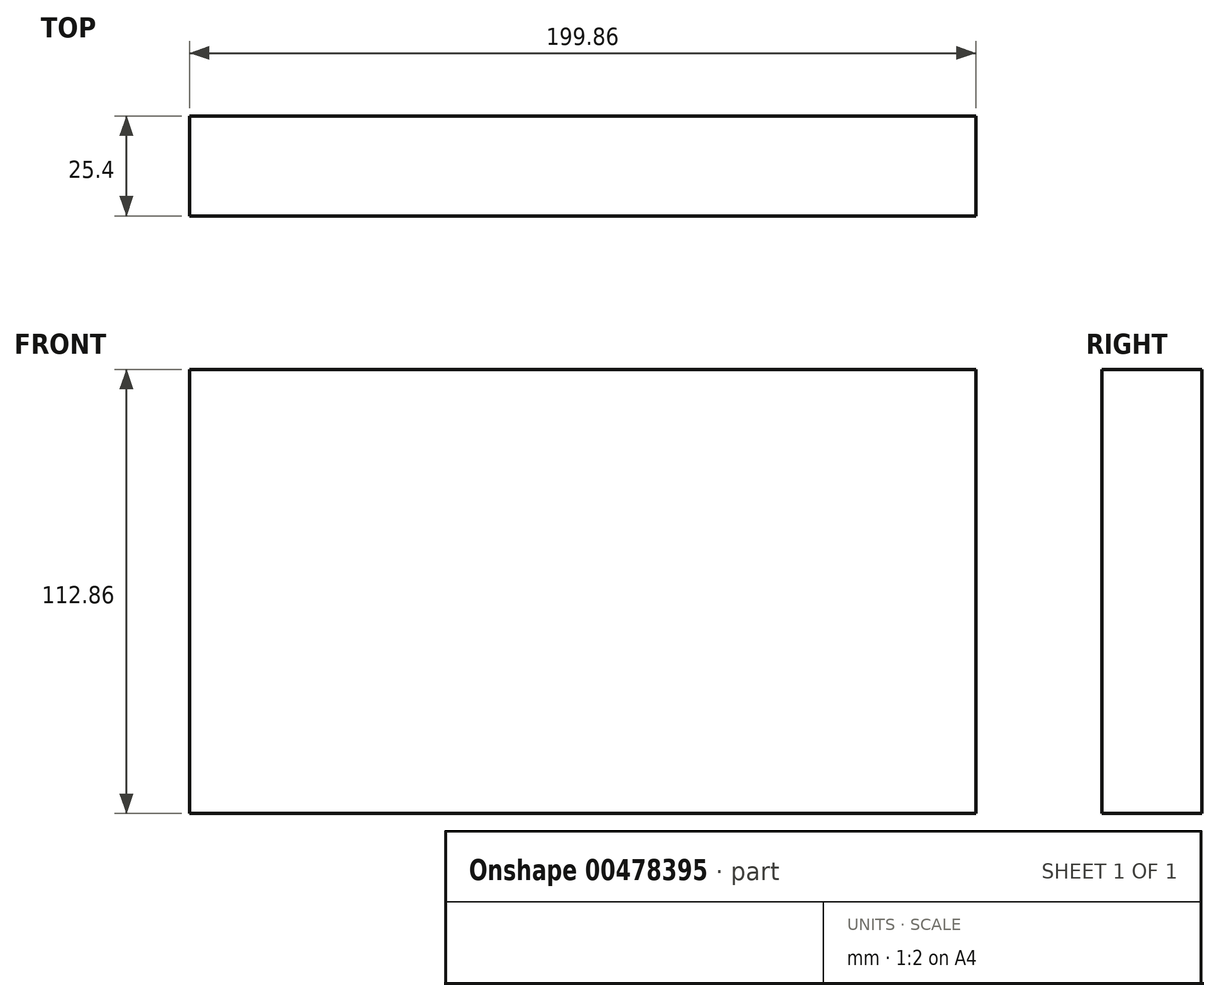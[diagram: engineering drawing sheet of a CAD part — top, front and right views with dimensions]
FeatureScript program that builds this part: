
annotation { "Feature Type Name" : "Feature", "Feature Type Description" : "" }
export const myFeature = defineFeature(function(context is Context, id is Id, definition is map)
    precondition{}
    {
        {
            var Q0;
            Q0=qCreatedBy(makeId("Front.planeOp"),FACE);
            var sketch = newSketch(context, id + "F0", { "sketchPlane" : qUnion([Q0])});
            skLineSegment(sketch, "E0.bottom", {"start": v(-97.72, 53.52) * mm, "end": v(102.14, 53.52) * mm});
            skLineSegment(sketch, "E0.top", {"start": v(-97.72, -59.34) * mm, "end": v(102.14, -59.34) * mm});
            skLineSegment(sketch, "E0.left", {"start": v(-97.72, 53.52) * mm, "end": v(-97.72, -59.34) * mm});
            skLineSegment(sketch, "E0.right", {"start": v(102.14, 53.52) * mm, "end": v(102.14, -59.34) * mm});
            skSolve(sketch);
        }
        {
            var Q0;
            Q0 = qSketchRegion(id + "F0", true);
            extrude(context, id + "F1", {"entities" : qUnion([Q0]), "depth" : 25.4 * mm});
        }
    });
